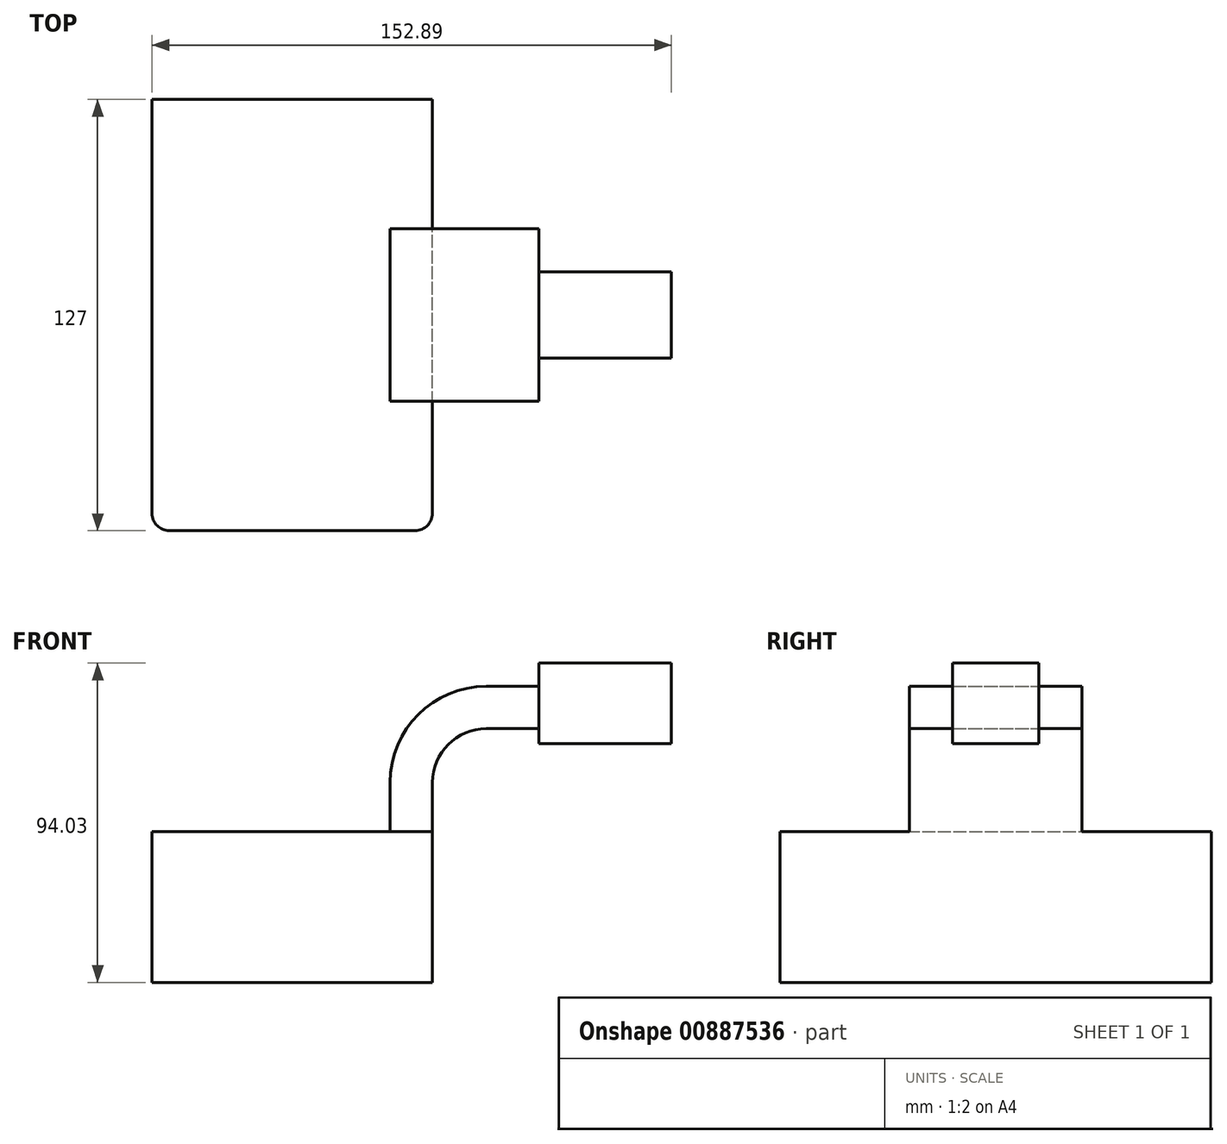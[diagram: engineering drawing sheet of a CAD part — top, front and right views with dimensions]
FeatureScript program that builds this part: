
annotation { "Feature Type Name" : "Feature", "Feature Type Description" : "" }
export const myFeature = defineFeature(function(context is Context, id is Id, definition is map)
    precondition{}
    {
        {
            var Q0;
            Q0=qCreatedBy(makeId("Front.planeOp"),FACE);
            var sketch = newSketch(context, id + "F0", { "sketchPlane" : qUnion([Q0])});
            skLineSegment(sketch, "E0.bottom", {"start": v(41.27, 22.22) * mm, "end": v(-41.27, 22.23) * mm});
            skLineSegment(sketch, "E0.top", {"start": v(41.27, -22.23) * mm, "end": v(-41.28, -22.22) * mm});
            skLineSegment(sketch, "E0.left", {"start": v(41.27, 22.22) * mm, "end": v(41.27, -22.23) * mm});
            skLineSegment(sketch, "E0.right", {"start": v(-41.27, 22.23) * mm, "end": v(-41.27, -22.22) * mm});
            skPoint(sketch, "E0.middle", {"position": v(0, 0) * mm});
            skPoint(sketch, "E1.middle", {"position": v(104.77, 55.9) * mm});
            skLineSegment(sketch, "E2", {"start": v(41.27, 22.22) * mm, "end": v(41.27, 36.62) * mm});
            skArc(sketch, "E3", {"start": v(41.27, 36.62) * mm, "mid": v(45.92, 47.85) * mm, "end": v(57.15, 52.5) * mm});
            skLineSegment(sketch, "E4", {"start": v(57.15, 52.5) * mm, "end": v(91.32, 52.5) * mm});
            skLineSegment(sketch, "E5.0", {"start": v(57.15, 64.94) * mm, "end": v(91.32, 64.94) * mm});
            skArc(sketch, "E5.1", {"start": v(28.83, 36.62) * mm, "mid": v(37.12, 56.65) * mm, "end": v(57.15, 64.94) * mm});
            skLineSegment(sketch, "E5.2", {"start": v(28.83, 8.69) * mm, "end": v(28.83, 36.62) * mm});
            skFitSpline(sketch, "E6", {"points": [v(-41.28, 22.23) * mm, v(57.15, 64.94) * mm], "startDerivative": vector(57.65, 87.3) * mm, "endDerivative": vector(125.64, -0.98) * mm});
            skLineSegment(sketch, "E7.bottom", {"start": v(111.62, 71.8) * mm, "end": v(72.65, 71.8) * mm});
            skLineSegment(sketch, "E7.top", {"start": v(111.62, 48.08) * mm, "end": v(72.65, 48.08) * mm});
            skLineSegment(sketch, "E7.left", {"start": v(111.62, 71.8) * mm, "end": v(111.62, 48.08) * mm});
            skLineSegment(sketch, "E7.right", {"start": v(72.65, 71.8) * mm, "end": v(72.65, 48.08) * mm});
            skPoint(sketch, "E7.middle", {"position": v(92.14, 59.94) * mm});
            skSolve(sketch);
        }
        {
            var Q0;
            Q0=makeQuery(id+"F0.imprint","IMPRINT",FACE,{"disambiguationData":[TD([[makeQuery(id+"F0.imprint","IMPRINT",EDGE,{"derivedFrom":sQuery(id+"F0.wireOp",EDGE,"E0.top")}),-1.0]])]});
            extrude(context, id + "F1", {"entities" : qUnion([Q0]), "endBound" : BoundingType.SYMMETRIC, "depth" : 127 * mm, "offsetDistance" : 25.4 * mm});
        }
        {
            var Q0;
            {var subQ1=sQuery(id+"F0.wireOp",EDGE,"E2");Q0=makeQuery(id+"F0.imprint","IMPRINT",FACE,{"disambiguationData":[TD([[makeQuery(id+"F0.imprint","IMPRINT",EDGE,{"derivedFrom":subQ1}),1.0]])]});}
            extrude(context, id + "F2", {"entities" : qUnion([Q0]), "operationType" : NewBodyOperationType.ADD, "endBound" : BoundingType.SYMMETRIC, "depth" : 50.8 * mm, "offsetDistance" : 25.4 * mm});
        }
        {
            var Q0;
            {var subQ4=sQuery(id+"F0.wireOp",EDGE,"E5.1");Q0=makeQuery(id+"F0.imprint","IMPRINT",FACE,{"disambiguationData":[TD([[makeQuery(id+"F0.imprint","IMPRINT",EDGE,{"derivedFrom":subQ4}),1.0]])]});}
            extrude(context, id + "F3", {"entities" : qUnion([Q0]), "operationType" : NewBodyOperationType.ADD, "endBound" : BoundingType.SYMMETRIC, "depth" : 15.88 * mm, "offsetDistance" : 25.4 * mm});
        }
        {
            var Q0;
            Q0=makeQuery(id+"F1.opExtrude","CAP_EDGE",EDGE,{"disambiguationData":[OSD([sQuery(id+"F0.wireOp",EDGE,"E0.left")])],"isStart":false});
            var Q1;
            Q1=makeQuery(id+"F1.opExtrude","CAP_EDGE",EDGE,{"disambiguationData":[OSD([sQuery(id+"F0.wireOp",EDGE,"E0.right")])],"isStart":false});
            fillet(context, id + "F4", {"entities" : qUnion([Q0, Q1]), "radius" : 5.08 * mm, "tangentPropagation" : true, "allowEdgeOverflow" : false});
        }
        {
            var Q0;
            {var subQ1=sQuery(id+"F0.wireOp",EDGE,"E7.bottom");Q0=makeQuery(id+"F0.imprint","IMPRINT",FACE,{"disambiguationData":[TD([[makeQuery(id+"F0.imprint","IMPRINT",EDGE,{"derivedFrom":subQ1}),1.0]])]});}
            extrude(context, id + "F5", {"entities" : qUnion([Q0]), "operationType" : NewBodyOperationType.ADD, "endBound" : BoundingType.SYMMETRIC, "depth" : 25.4 * mm, "offsetDistance" : 25.4 * mm});
        }
    });
